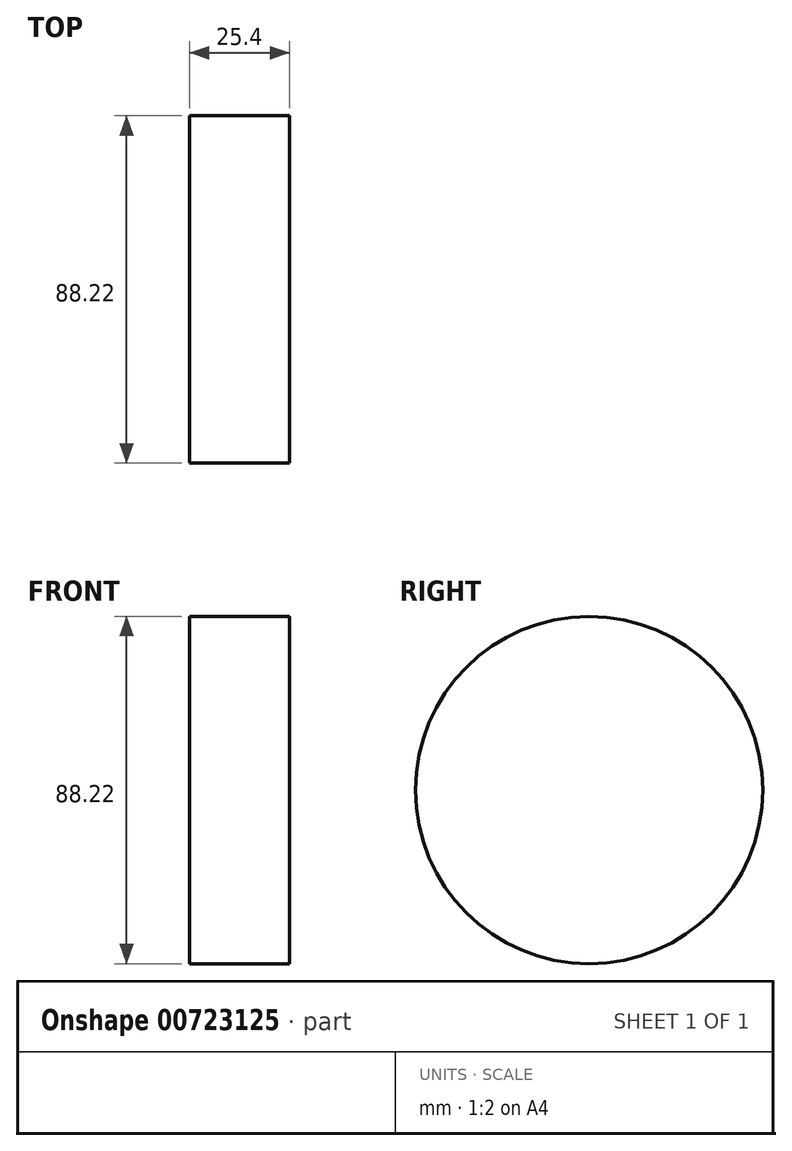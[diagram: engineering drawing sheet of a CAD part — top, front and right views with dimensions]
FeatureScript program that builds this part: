
annotation { "Feature Type Name" : "Feature", "Feature Type Description" : "" }
export const myFeature = defineFeature(function(context is Context, id is Id, definition is map)
    precondition{}
    {
        {
            var Q0;
            Q0=qCreatedBy(makeId("Right.planeOp"),FACE);
            var sketch = newSketch(context, id + "F0", { "sketchPlane" : qUnion([Q0])});
            skCircle(sketch, "E0", {"center": v(0, 0) * mm, "radius": 44.1 * mm});
            skSolve(sketch);
        }
        {
            var Q0;
            Q0=sQuery(id+"F0.wireOp",EDGE,"E0");
            extrude(context, id + "F1", {"bodyType" : ToolBodyType.SURFACE, "surfaceEntities" : qUnion([Q0]), "depth" : 25.4 * mm, "offsetDistance" : 25.4 * mm});
        }
    });
